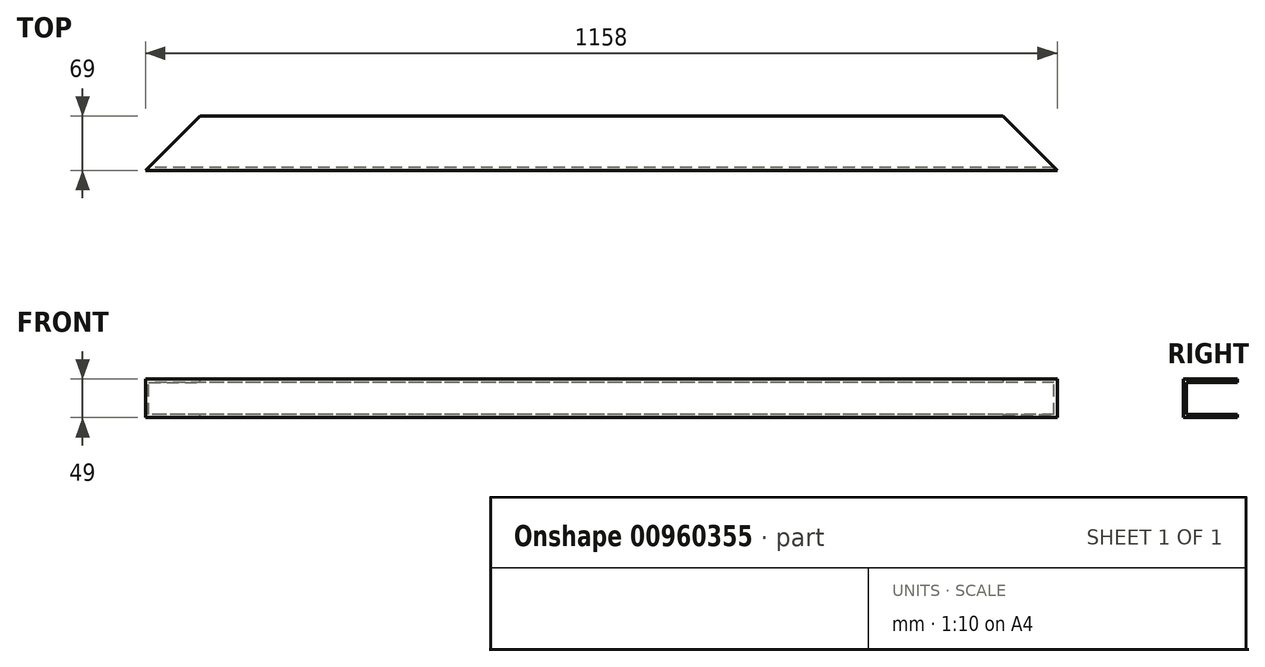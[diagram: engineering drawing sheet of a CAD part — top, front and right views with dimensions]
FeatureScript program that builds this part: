
annotation { "Feature Type Name" : "Feature", "Feature Type Description" : "" }
export const myFeature = defineFeature(function(context is Context, id is Id, definition is map)
    precondition{}
    {
        {
            var Q0;
            Q0=qCreatedBy(makeId("Right.planeOp"),FACE);
            var sketch = newSketch(context, id + "F0", { "sketchPlane" : qUnion([Q0])});
            skLineSegment(sketch, "E0.bottom", {"start": v(-34.5, 24.5) * mm, "end": v(34.5, 24.5) * mm});
            skLineSegment(sketch, "E0.top", {"start": v(-34.5, -24.5) * mm, "end": v(34.5, -24.5) * mm});
            skLineSegment(sketch, "E0.left", {"start": v(-34.5, 24.5) * mm, "end": v(-34.5, -24.5) * mm});
            skLineSegment(sketch, "E0.right", {"start": v(34.5, 24.5) * mm, "end": v(34.5, -24.5) * mm});
            skPoint(sketch, "E0.middle", {"position": v(0, 0) * mm});
            skSolve(sketch);
        }
        {
            var Q0;
            Q0 = qSketchRegion(id + "F0", true);
            extrude(context, id + "F1", {"entities" : qUnion([Q0]), "endBound" : BoundingType.SYMMETRIC, "depth" : 1158 * mm, "offsetDistance" : 25 * mm});
        }
        {
            var Q0;
            Q0=makeQuery(id+"F1.opExtrude","CAP_FACE",FACE,{"disambiguationData":[OSD([sQuery(id+"F0.wireOp",EDGE,"E0.bottom"),sQuery(id+"F0.wireOp",EDGE,"E0.top"),sQuery(id+"F0.wireOp",EDGE,"E0.left"),sQuery(id+"F0.wireOp",EDGE,"E0.right")])],"isStart":false});
            var Q1;
            Q1=makeQuery(id+"F1.opExtrude","SWEPT_FACE",FACE,{"disambiguationData":[OSD([sQuery(id+"F0.wireOp",EDGE,"E0.right")])]});
            var Q2;
            Q2=makeQuery(id+"F1.opExtrude","CAP_FACE",FACE,{"disambiguationData":[OSD([sQuery(id+"F0.wireOp",EDGE,"E0.bottom"),sQuery(id+"F0.wireOp",EDGE,"E0.top"),sQuery(id+"F0.wireOp",EDGE,"E0.left"),sQuery(id+"F0.wireOp",EDGE,"E0.right")])],"isStart":true});
            shell(context, id + "F2", {"entities" : qUnion([Q0, Q1, Q2]), "thickness" : 4 * mm});
        }
        {
            var Q0;
            Q0=makeQuery(id+"F1.opExtrude","CAP_EDGE",EDGE,{"disambiguationData":[OSD([sQuery(id+"F0.wireOp",EDGE,"E0.right")])],"isStart":false});
            var Q1;
            {var subQ0=sQuery(id+"F0.wireOp",EDGE,"E0.right");Q1=makeQuery(id+"F2.opShell","OFFSET_EDGE",EDGE,{"disambiguationData":[OSD([subQ0]),TDD([makeQuery(id+"F1.opExtrude","CAP_EDGE",EDGE,{"disambiguationData":[OSD([subQ0])],"isStart":false})])]});}
            var Q2;
            Q2=makeQuery(id+"F1.opExtrude","CAP_EDGE",EDGE,{"disambiguationData":[OSD([sQuery(id+"F0.wireOp",EDGE,"E0.right")])],"isStart":true});
            chamfer(context, id + "F3", {"entities" : qUnion([Q0, Q1, Q2]), "width" : 69 * mm, "tangentPropagation" : true});
        }
    });
